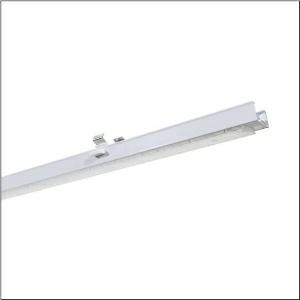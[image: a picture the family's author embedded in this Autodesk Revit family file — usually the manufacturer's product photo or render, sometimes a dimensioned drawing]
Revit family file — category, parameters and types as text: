
# Revit family: trunking_flex_31_51re11db4cb
name_source: partatom
category: Lighting Fixtures
units: mm (PartAtom-declared; Revit-internal decimal feet)

## family parameters
Cut with Voids When Loaded = No
Host = Face
Light Source = No
Part Type = Normal
Room Calculation Point = No
Round Connector Dimension = Use Diameter
Shared = No

## types (1)
- Trunking Flex 31 (1 x LED, 11500 lm, 66 W, 4000K)
    Apparent Load = 66 VA
    CIE Flux Codes = 83 93 98 100 100
    Color Rendering = 80
    Color Temperature = 4000K
    Default Elevation = 1800 mm
    Description = Trunking Flex 31, luminaire insert, of extruded aluminium section, coated, traffic white (RAL 9016), length: 1.472mm, width: 91mm, height: 53mm, LED rated luminous flux: 11.500lm, light colour: 840, control gear: DALI 2, with system connector: socket, mains connection: 220..240V, AC, 50/60Hz, rated input power: 66W, primary light control with lens, of plastic, primary optical cover: cover, of PMMA, light emission: direct distribution, protection rating (complete): IP20, insulation class (complete): insulation class I (protective earthing), certification: CE, UKCA, impact resistance: IK02, permissible ambient temperature for indoor applications: -20..+40°C, packaging unit: 1 piece
    Height = 58 mm
    Lamp = 1 x LED
    Lamp Light Flux = 11500 lm
    Lamp Power = 66 W
    Lamp count = 1
    Length = 1472 mm
    Luminous efficacy = 174 lm/W
    Manufacturer = Siteco
    ModVariant = No
    Model = 51RE11DB4CB
    Mounting Place = Ceiling
    Mounting Type = Pendant
    Number of Poles = 1
    OnlyDefault = Yes
    Power Factor = 1
    Product Name = Trunking Flex 31
    Product group = luminaire insert
    ProductGroupID = 902
    Protection Class = Protection class I
    Protection Degree = IP 20
    RLX_Detail_Level = 1
    RLX_Emergency_Light_Flux = 0 lm
    RLX_Emergency_Type = 0
    RLX_Emergency_Type_DB = No
    RlxData = <blob elided: 19485 chars, md5=6fbab8e6>
    Socket = socket
    Standby Power = 0 W
    System Light Flux = 11500 lm
    System Power = 66 W
    Type Comments = Product without accessories
    Type Image = l_1266702.jpg
    URL = http://relux.com
    VarID = ---
    Voltage = 0 V
    Weight = 0.00 kg
    Width = 65 mm

## geometry (parser evidence)
native form markers: Blend x4, Sweep x10
no freeform markers — native parametric forms only
